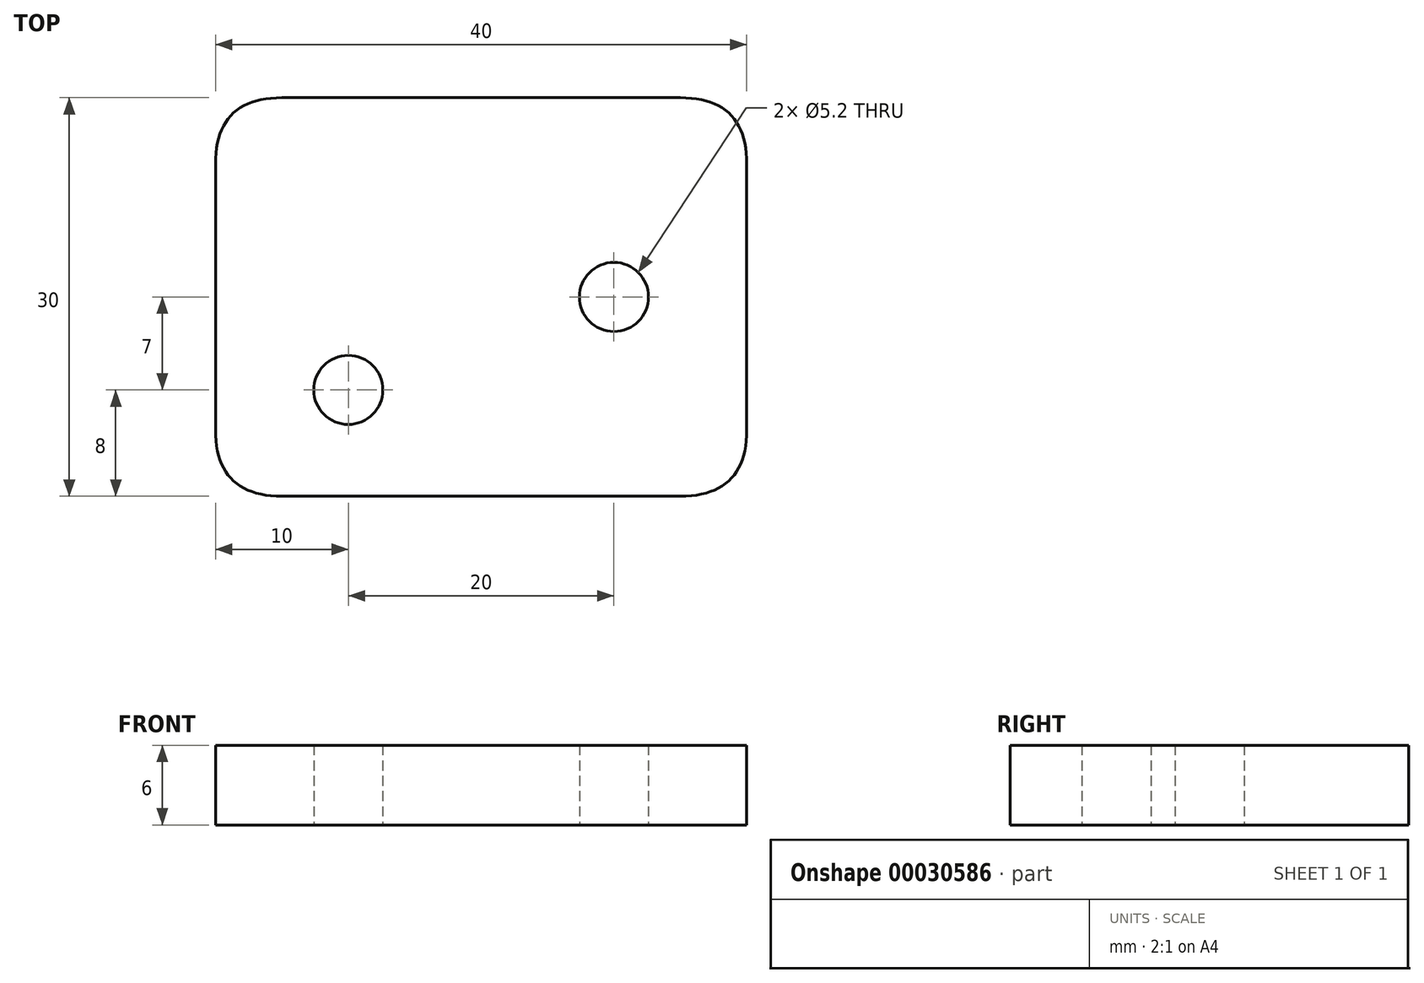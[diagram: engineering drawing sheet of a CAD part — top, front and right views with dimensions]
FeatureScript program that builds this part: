
annotation { "Feature Type Name" : "Feature", "Feature Type Description" : "" }
export const myFeature = defineFeature(function(context is Context, id is Id, definition is map)
    precondition{}
    {
        {
            var Q0;
            Q0=qCreatedBy(makeId("Top.planeOp"),FACE);
            var sketch = newSketch(context, id + "F0", { "sketchPlane" : qUnion([Q0])});
            skLineSegment(sketch, "E0.bottom", {"start": v(-20, 15) * mm, "end": v(20, 15) * mm});
            skLineSegment(sketch, "E0.top", {"start": v(-20, -15) * mm, "end": v(20, -15) * mm});
            skLineSegment(sketch, "E0.left", {"start": v(-20, 15) * mm, "end": v(-20, -15) * mm});
            skLineSegment(sketch, "E0.right", {"start": v(20, 15) * mm, "end": v(20, -15) * mm});
            skCircle(sketch, "E1", {"center": v(10, 0) * mm, "radius": 2.6 * mm});
            skCircle(sketch, "E2", {"center": v(-10, -7) * mm, "radius": 2.6 * mm});
            skSolve(sketch);
        }
        {
            var Q0;
            Q0=makeQuery(id+"F0.imprint","IMPRINT",FACE,{"disambiguationData":[TD([[makeQuery(id+"F0.imprint","IMPRINT",EDGE,{"derivedFrom":sQuery(id+"F0.wireOp",EDGE,"E0.bottom")}),-1.0]])]});
            extrude(context, id + "F1", {"entities" : qUnion([Q0]), "depth" : 6 * mm});
        }
        {
            var Q0;
            Q0=makeQuery(id+"F1.opExtrude","SWEPT_EDGE",EDGE,{"disambiguationData":[OSD([sQuery(id+"F0.wireOp",EDGE,"E0.top"),sQuery(id+"F0.wireOp",EDGE,"E0.left")])]});
            var Q1;
            Q1=makeQuery(id+"F1.opExtrude","SWEPT_EDGE",EDGE,{"disambiguationData":[OSD([sQuery(id+"F0.wireOp",EDGE,"E0.top"),sQuery(id+"F0.wireOp",EDGE,"E0.right")])]});
            var Q2;
            Q2=makeQuery(id+"F1.opExtrude","SWEPT_EDGE",EDGE,{"disambiguationData":[OSD([sQuery(id+"F0.wireOp",EDGE,"E0.bottom"),sQuery(id+"F0.wireOp",EDGE,"E0.right")])]});
            var Q3;
            Q3=makeQuery(id+"F1.opExtrude","SWEPT_EDGE",EDGE,{"disambiguationData":[OSD([sQuery(id+"F0.wireOp",EDGE,"E0.bottom"),sQuery(id+"F0.wireOp",EDGE,"E0.left")])]});
            fillet(context, id + "F2", {"entities" : qUnion([Q0, Q1, Q2, Q3]), "radius" : 5 * mm, "tangentPropagation" : true, "rho" : 0.5, "crossSection" : FilletCrossSection.CONIC, "allowEdgeOverflow" : false});
        }
    });
